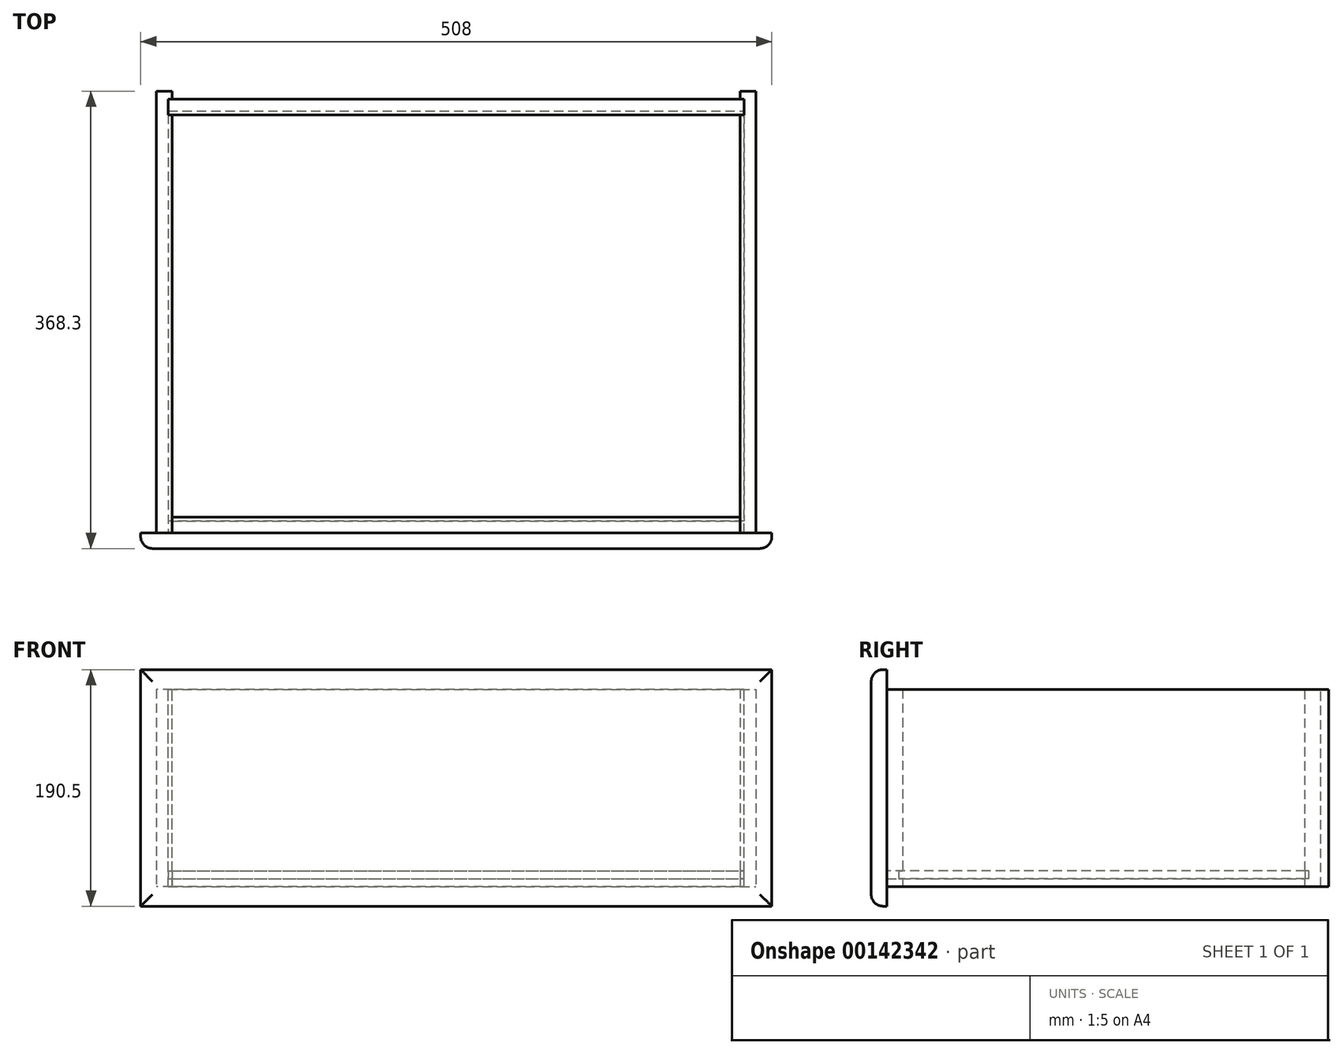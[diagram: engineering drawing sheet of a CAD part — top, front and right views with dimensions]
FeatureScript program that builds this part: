
annotation { "Feature Type Name" : "Feature", "Feature Type Description" : "" }
export const myFeature = defineFeature(function(context is Context, id is Id, definition is map)
    precondition{}
    {
        {
            var Q0;
            Q0=qCreatedBy(makeId("Front.planeOp"),FACE);
            var sketch = newSketch(context, id + "F0", { "sketchPlane" : qUnion([Q0])});
            skLineSegment(sketch, "E0.bottom", {"start": v(-262.84, 81.63) * mm, "end": v(245.16, 81.63) * mm});
            skLineSegment(sketch, "E0.top", {"start": v(-262.84, -108.87) * mm, "end": v(245.16, -108.87) * mm});
            skLineSegment(sketch, "E0.left", {"start": v(-262.84, 81.63) * mm, "end": v(-262.84, -108.87) * mm});
            skLineSegment(sketch, "E0.right", {"start": v(245.16, 81.63) * mm, "end": v(245.16, -108.87) * mm});
            skSolve(sketch);
        }
        {
            var Q0;
            Q0=makeQuery(id+"F0.imprint","IMPRINT",FACE,{"disambiguationData":[TD([[makeQuery(id+"F0.imprint","IMPRINT",EDGE,{"derivedFrom":sQuery(id+"F0.wireOp",EDGE,"E0.bottom")}),-1.0]])]});
            extrude(context, id + "F1", {"entities" : qUnion([Q0]), "depth" : 12.7 * mm});
        }
        {
            var Q0;
            Q0=makeQuery(id+"F1.opExtrude","CAP_EDGE",EDGE,{"disambiguationData":[OSD([sQuery(id+"F0.wireOp",EDGE,"E0.bottom")])],"isStart":false});
            var Q1;
            Q1=makeQuery(id+"F1.opExtrude","CAP_EDGE",EDGE,{"disambiguationData":[OSD([sQuery(id+"F0.wireOp",EDGE,"E0.left")])],"isStart":false});
            var Q2;
            Q2=makeQuery(id+"F1.opExtrude","CAP_EDGE",EDGE,{"disambiguationData":[OSD([sQuery(id+"F0.wireOp",EDGE,"E0.top")])],"isStart":false});
            var Q3;
            Q3=makeQuery(id+"F1.opExtrude","CAP_EDGE",EDGE,{"disambiguationData":[OSD([sQuery(id+"F0.wireOp",EDGE,"E0.right")])],"isStart":false});
            fillet(context, id + "F2", {"entities" : qUnion([Q0, Q1, Q2, Q3]), "radius" : 9.52 * mm, "tangentPropagation" : true, "allowEdgeOverflow" : false});
        }
        {
            var Q0;
            Q0=makeQuery(id+"F1.opExtrude","CAP_FACE",FACE,{"disambiguationData":[OSD([sQuery(id+"F0.wireOp",EDGE,"E0.bottom"),sQuery(id+"F0.wireOp",EDGE,"E0.top"),sQuery(id+"F0.wireOp",EDGE,"E0.left"),sQuery(id+"F0.wireOp",EDGE,"E0.right")])],"isStart":true});
            var sketch = newSketch(context, id + "F3", { "sketchPlane" : qUnion([Q0])});
            skLineSegment(sketch, "E1.bottom", {"start": v(-219.76, 65.76) * mm, "end": v(237.44, 65.76) * mm});
            skLineSegment(sketch, "E1.top", {"start": v(-219.76, -93) * mm, "end": v(237.44, -93) * mm});
            skLineSegment(sketch, "E1.left", {"start": v(-219.76, 65.76) * mm, "end": v(-219.76, -93) * mm});
            skLineSegment(sketch, "E1.right", {"start": v(237.44, 65.76) * mm, "end": v(237.44, -93) * mm});
            skSolve(sketch);
        }
        {
            var Q0;
            Q0=makeQuery(id+"F3.imprint","IMPRINT",FACE,{"disambiguationData":[TD([[makeQuery(id+"F3.imprint","IMPRINT",EDGE,{"derivedFrom":sQuery(id+"F3.wireOp",EDGE,"E1.bottom")}),-1.0]])]});
            extrude(context, id + "F4", {"entities" : qUnion([Q0]), "operationType" : NewBodyOperationType.ADD, "depth" : 12.7 * mm});
        }
        {
            var Q0;
            Q0=makeQuery(id+"F1.opExtrude","CAP_FACE",FACE,{"disambiguationData":[OSD([sQuery(id+"F0.wireOp",EDGE,"E0.bottom"),sQuery(id+"F0.wireOp",EDGE,"E0.top"),sQuery(id+"F0.wireOp",EDGE,"E0.left"),sQuery(id+"F0.wireOp",EDGE,"E0.right")])],"isStart":true});
            var sketch = newSketch(context, id + "F5", { "sketchPlane" : qUnion([Q0])});
            skLineSegment(sketch, "E2.bottom", {"start": v(-219.76, 65.76) * mm, "end": v(-232.46, 65.76) * mm});
            skLineSegment(sketch, "E2.top", {"start": v(-219.76, -93) * mm, "end": v(-232.46, -93) * mm});
            skLineSegment(sketch, "E2.left", {"start": v(-219.76, 65.76) * mm, "end": v(-219.76, -93) * mm});
            skLineSegment(sketch, "E2.right", {"start": v(-232.46, 65.76) * mm, "end": v(-232.46, -93) * mm});
            skSolve(sketch);
        }
        {
            var Q0;
            Q0=makeQuery(id+"F5.imprint","IMPRINT",FACE,{"disambiguationData":[TD([[makeQuery(id+"F5.imprint","IMPRINT",EDGE,{"derivedFrom":sQuery(id+"F5.wireOp",EDGE,"E2.bottom")}),1.0]])]});
            extrude(context, id + "F6", {"entities" : qUnion([Q0]), "depth" : 355.6 * mm});
        }
        {
            var Q0;
            Q0=makeQuery(id+"F1.opExtrude","CAP_FACE",FACE,{"disambiguationData":[OSD([sQuery(id+"F0.wireOp",EDGE,"E0.bottom"),sQuery(id+"F0.wireOp",EDGE,"E0.top"),sQuery(id+"F0.wireOp",EDGE,"E0.left"),sQuery(id+"F0.wireOp",EDGE,"E0.right")])],"isStart":true});
            var sketch = newSketch(context, id + "F7", { "sketchPlane" : qUnion([Q0])});
            skLineSegment(sketch, "E3.bottom", {"start": v(237.44, 65.76) * mm, "end": v(250.14, 65.76) * mm});
            skLineSegment(sketch, "E3.top", {"start": v(237.44, -93) * mm, "end": v(250.14, -93) * mm});
            skLineSegment(sketch, "E3.left", {"start": v(237.44, 65.76) * mm, "end": v(237.44, -93) * mm});
            skLineSegment(sketch, "E3.right", {"start": v(250.14, 65.76) * mm, "end": v(250.14, -93) * mm});
            skSolve(sketch);
        }
        {
            var Q0;
            Q0=makeQuery(id+"F7.imprint","IMPRINT",FACE,{"disambiguationData":[TD([[makeQuery(id+"F7.imprint","IMPRINT",EDGE,{"derivedFrom":sQuery(id+"F7.wireOp",EDGE,"E3.bottom")}),-1.0]])]});
            extrude(context, id + "F8", {"entities" : qUnion([Q0]), "depth" : 355.6 * mm});
        }
        {
            var Q0;
            Q0=makeQuery(id+"F8.opExtrude","SWEPT_FACE",FACE,{"disambiguationData":[OSD([sQuery(id+"F7.wireOp",EDGE,"E3.bottom")])]});
            var sketch = newSketch(context, id + "F9", { "sketchPlane" : qUnion([Q0])});
            skLineSegment(sketch, "E4", {"start": v(-237.44, 349.25) * mm, "end": v(-240.62, 349.25) * mm});
            skLineSegment(sketch, "E5", {"start": v(-240.62, 349.25) * mm, "end": v(-240.62, 336.55) * mm});
            skLineSegment(sketch, "E6", {"start": v(-240.62, 336.55) * mm, "end": v(-237.44, 336.55) * mm});
            skSolve(sketch);
        }
        {
            var Q0;
            {var subQ0=sQuery(id+"F9.wireOp",EDGE,"E4");Q0=makeQuery(id+"F9.imprint","IMPRINT",FACE,{"disambiguationData":[TD([[makeQuery(id+"F9.imprint","IMPRINT",EDGE,{"derivedFrom":subQ0}),1.0]])]});}
            extrude(context, id + "F10", {"entities" : qUnion([Q0]), "operationType" : NewBodyOperationType.REMOVE, "endBound" : BoundingType.THROUGH_ALL, "oppositeDirection" : true, "depth" : 25.4 * mm});
        }
        {
            var Q0;
            Q0=makeQuery(id+"F6.opExtrude","SWEPT_FACE",FACE,{"disambiguationData":[OSD([sQuery(id+"F5.wireOp",EDGE,"E2.bottom")])]});
            var sketch = newSketch(context, id + "F11", { "sketchPlane" : qUnion([Q0])});
            skLineSegment(sketch, "E7", {"start": v(219.76, 349.25) * mm, "end": v(222.93, 349.25) * mm});
            skLineSegment(sketch, "E8", {"start": v(222.93, 349.25) * mm, "end": v(222.93, 336.55) * mm});
            skLineSegment(sketch, "E9", {"start": v(222.93, 336.55) * mm, "end": v(219.76, 336.55) * mm});
            skSolve(sketch);
        }
        {
            var Q0;
            {var subQ0=sQuery(id+"F11.wireOp",EDGE,"E7");Q0=makeQuery(id+"F11.imprint","IMPRINT",FACE,{"disambiguationData":[TD([[makeQuery(id+"F11.imprint","IMPRINT",EDGE,{"derivedFrom":subQ0}),-1.0]])]});}
            extrude(context, id + "F12", {"entities" : qUnion([Q0]), "operationType" : NewBodyOperationType.REMOVE, "endBound" : BoundingType.THROUGH_ALL, "oppositeDirection" : true, "depth" : 25.4 * mm});
        }
        {
            var Q0;
            Q0=makeQuery(id+"F8.opExtrude","SWEPT_FACE",FACE,{"disambiguationData":[OSD([sQuery(id+"F7.wireOp",EDGE,"E3.bottom")])]});
            var sketch = newSketch(context, id + "F13", { "sketchPlane" : qUnion([Q0])});
            skLineSegment(sketch, "E10.bottom", {"start": v(-240.62, 349.25) * mm, "end": v(222.93, 349.25) * mm});
            skLineSegment(sketch, "E10.top", {"start": v(-240.62, 336.55) * mm, "end": v(222.93, 336.55) * mm});
            skLineSegment(sketch, "E10.left", {"start": v(-240.62, 349.25) * mm, "end": v(-240.62, 336.55) * mm});
            skLineSegment(sketch, "E10.right", {"start": v(222.93, 349.25) * mm, "end": v(222.93, 336.55) * mm});
            skSolve(sketch);
        }
        {
            var Q0;
            {var subQ0=sQuery(id+"F13.wireOp",EDGE,"E10.left");Q0=makeQuery(id+"F13.imprint","IMPRINT",FACE,{"disambiguationData":[TD([[makeQuery(id+"F13.imprint","IMPRINT",EDGE,{"derivedFrom":subQ0}),1.0]])]});}
            extrude(context, id + "F14", {"entities" : qUnion([Q0]), "oppositeDirection" : true, "depth" : 158.75 * mm});
        }
        {
            var Q0;
            Q0=makeQuery(id+"F14.opExtrude","SWEPT_FACE",FACE,{"disambiguationData":[OSD([sQuery(id+"F13.wireOp",EDGE,"E10.top")])]});
            var sketch = newSketch(context, id + "F15", { "sketchPlane" : qUnion([Q0])});
            skLineSegment(sketch, "E11.bottom", {"start": v(-240.62, -86.64) * mm, "end": v(222.93, -86.64) * mm});
            skLineSegment(sketch, "E11.top", {"start": v(-240.62, -80.3) * mm, "end": v(222.93, -80.3) * mm});
            skLineSegment(sketch, "E11.left", {"start": v(-240.62, -86.64) * mm, "end": v(-240.62, -80.3) * mm});
            skLineSegment(sketch, "E11.right", {"start": v(222.93, -86.64) * mm, "end": v(222.93, -80.3) * mm});
            skSolve(sketch);
        }
        {
            var Q0;
            Q0=makeQuery(id+"F15.imprint","IMPRINT",FACE,{"disambiguationData":[TD([[makeQuery(id+"F15.imprint","IMPRINT",EDGE,{"derivedFrom":sQuery(id+"F15.wireOp",EDGE,"E11.bottom")}),1.0]])]});
            extrude(context, id + "F16", {"entities" : qUnion([Q0]), "operationType" : NewBodyOperationType.REMOVE, "oppositeDirection" : true, "depth" : 3.17 * mm});
        }
        {
            var Q0;
            {var subQ1=sQuery(id+"F5.wireOp",EDGE,"E2.left");Q0=makeQuery(id+"F12.boolean.opBoolean","SPLIT",FACE,{"disambiguationData":[TD([makeQuery(id+"F12.opExtrude","SWEPT_FACE",FACE,{"disambiguationData":[OSD([sQuery(id+"F11.wireOp",EDGE,"E9")])]})])],"derivedFrom":makeQuery(id+"F6.opExtrude","SWEPT_FACE",FACE,{"disambiguationData":[OSD([subQ1])]})});}
            var sketch = newSketch(context, id + "F17", { "sketchPlane" : qUnion([Q0])});
            skLineSegment(sketch, "E12.bottom", {"start": v(0, -80.3) * mm, "end": v(-336.55, -80.3) * mm});
            skLineSegment(sketch, "E12.top", {"start": v(0, -86.64) * mm, "end": v(-336.55, -86.64) * mm});
            skLineSegment(sketch, "E12.left", {"start": v(0, -80.3) * mm, "end": v(0, -86.64) * mm});
            skLineSegment(sketch, "E12.right", {"start": v(-336.55, -80.3) * mm, "end": v(-336.55, -86.64) * mm});
            skSolve(sketch);
        }
        {
            var Q0;
            Q0=makeQuery(id+"F17.imprint","IMPRINT",FACE,{"disambiguationData":[TD([[makeQuery(id+"F17.imprint","IMPRINT",EDGE,{"derivedFrom":sQuery(id+"F17.wireOp",EDGE,"E12.bottom")}),1.0]])]});
            extrude(context, id + "F18", {"entities" : qUnion([Q0]), "operationType" : NewBodyOperationType.REMOVE, "oppositeDirection" : true, "depth" : 3.17 * mm});
        }
        {
            var Q0;
            {var subQ1=sQuery(id+"F7.wireOp",EDGE,"E3.left");Q0=makeQuery(id+"F10.boolean.opBoolean","SPLIT",FACE,{"disambiguationData":[TD([makeQuery(id+"F10.opExtrude","SWEPT_FACE",FACE,{"disambiguationData":[OSD([sQuery(id+"F9.wireOp",EDGE,"E6")])]})])],"derivedFrom":makeQuery(id+"F8.opExtrude","SWEPT_FACE",FACE,{"disambiguationData":[OSD([subQ1])]})});}
            var sketch = newSketch(context, id + "F19", { "sketchPlane" : qUnion([Q0])});
            skLineSegment(sketch, "E13.top", {"start": v(0, -86.64) * mm, "end": v(5.25, -86.64) * mm});
            skLineSegment(sketch, "E13.left", {"start": v(0, -86.64) * mm, "end": v(0, -85.22) * mm});
            skLineSegment(sketch, "E14.bottom", {"start": v(336.55, -80.3) * mm, "end": v(0, -80.3) * mm});
            skLineSegment(sketch, "E14.top", {"start": v(336.55, -86.64) * mm, "end": v(0, -86.64) * mm});
            skLineSegment(sketch, "E14.left", {"start": v(336.55, -80.3) * mm, "end": v(336.55, -86.64) * mm});
            skLineSegment(sketch, "E14.right", {"start": v(0, -80.3) * mm, "end": v(0, -86.64) * mm});
            skSolve(sketch);
        }
        {
            var Q0;
            {var subQ5=sQuery(id+"F19.wireOp",EDGE,"E13.bottom");Q0=makeQuery(id+"F19.imprint","IMPRINT",FACE,{"disambiguationData":[TD([[makeQuery(id+"F19.imprint","IMPRINT",EDGE,{"derivedFrom":subQ5}),1.0]])]});}
            var Q1;
            {var subQ7=sQuery(id+"F19.wireOp",EDGE,"E14.bottom");Q1=makeQuery(id+"F19.imprint","IMPRINT",FACE,{"disambiguationData":[TD([[makeQuery(id+"F19.imprint","IMPRINT",EDGE,{"derivedFrom":subQ7}),1.0]])]});}
            extrude(context, id + "F20", {"entities" : qUnion([Q0, Q1]), "operationType" : NewBodyOperationType.REMOVE, "oppositeDirection" : true, "depth" : 3.17 * mm});
        }
        {
            var Q0;
            Q0=makeQuery(id+"F4.opExtrude","CAP_FACE",FACE,{"disambiguationData":[OSD([sQuery(id+"F3.wireOp",EDGE,"E1.bottom"),sQuery(id+"F3.wireOp",EDGE,"E1.top"),sQuery(id+"F3.wireOp",EDGE,"E1.left"),sQuery(id+"F3.wireOp",EDGE,"E1.right")])],"isStart":false});
            var sketch = newSketch(context, id + "F21", { "sketchPlane" : qUnion([Q0])});
            skLineSegment(sketch, "E15.bottom", {"start": v(237.44, -80.3) * mm, "end": v(-219.76, -80.3) * mm});
            skLineSegment(sketch, "E15.top", {"start": v(237.44, -86.64) * mm, "end": v(-219.76, -86.64) * mm});
            skLineSegment(sketch, "E15.left", {"start": v(237.44, -80.3) * mm, "end": v(237.44, -86.64) * mm});
            skLineSegment(sketch, "E15.right", {"start": v(-219.76, -80.3) * mm, "end": v(-219.76, -86.64) * mm});
            skSolve(sketch);
        }
        {
            var Q0;
            Q0=makeQuery(id+"F21.imprint","IMPRINT",FACE,{"disambiguationData":[TD([[makeQuery(id+"F21.imprint","IMPRINT",EDGE,{"derivedFrom":sQuery(id+"F21.wireOp",EDGE,"E15.bottom")}),1.0]])]});
            extrude(context, id + "F22", {"entities" : qUnion([Q0]), "operationType" : NewBodyOperationType.REMOVE, "oppositeDirection" : true, "depth" : 3.17 * mm});
        }
        {
            var Q0;
            Q0=makeQuery(id+"F16.boolean.opBoolean","COPY",FACE,{"derivedFrom":makeQuery(id+"F16.opExtrude","SWEPT_FACE",FACE,{"disambiguationData":[OSD([sQuery(id+"F15.wireOp",EDGE,"E11.bottom")])]})});
            var sketch = newSketch(context, id + "F23", { "sketchPlane" : qUnion([Q0])});
            skLineSegment(sketch, "E16.bottom", {"start": v(222.93, 339.73) * mm, "end": v(-240.62, 339.72) * mm});
            skLineSegment(sketch, "E16.top", {"start": v(222.93, 9.52) * mm, "end": v(-240.62, 9.52) * mm});
            skLineSegment(sketch, "E16.left", {"start": v(222.93, 339.73) * mm, "end": v(222.93, 9.52) * mm});
            skLineSegment(sketch, "E16.right", {"start": v(-240.62, 339.72) * mm, "end": v(-240.62, 9.52) * mm});
            skSolve(sketch);
        }
        {
            var Q0;
            {var subQ0=sQuery(id+"F23.wireOp",EDGE,"E16.top");Q0=makeQuery(id+"F23.imprint","IMPRINT",FACE,{"disambiguationData":[TD([[makeQuery(id+"F23.imprint","IMPRINT",EDGE,{"derivedFrom":subQ0}),-1.0]])]});}
            extrude(context, id + "F24", {"entities" : qUnion([Q0]), "depth" : 6.35 * mm});
        }
    });
